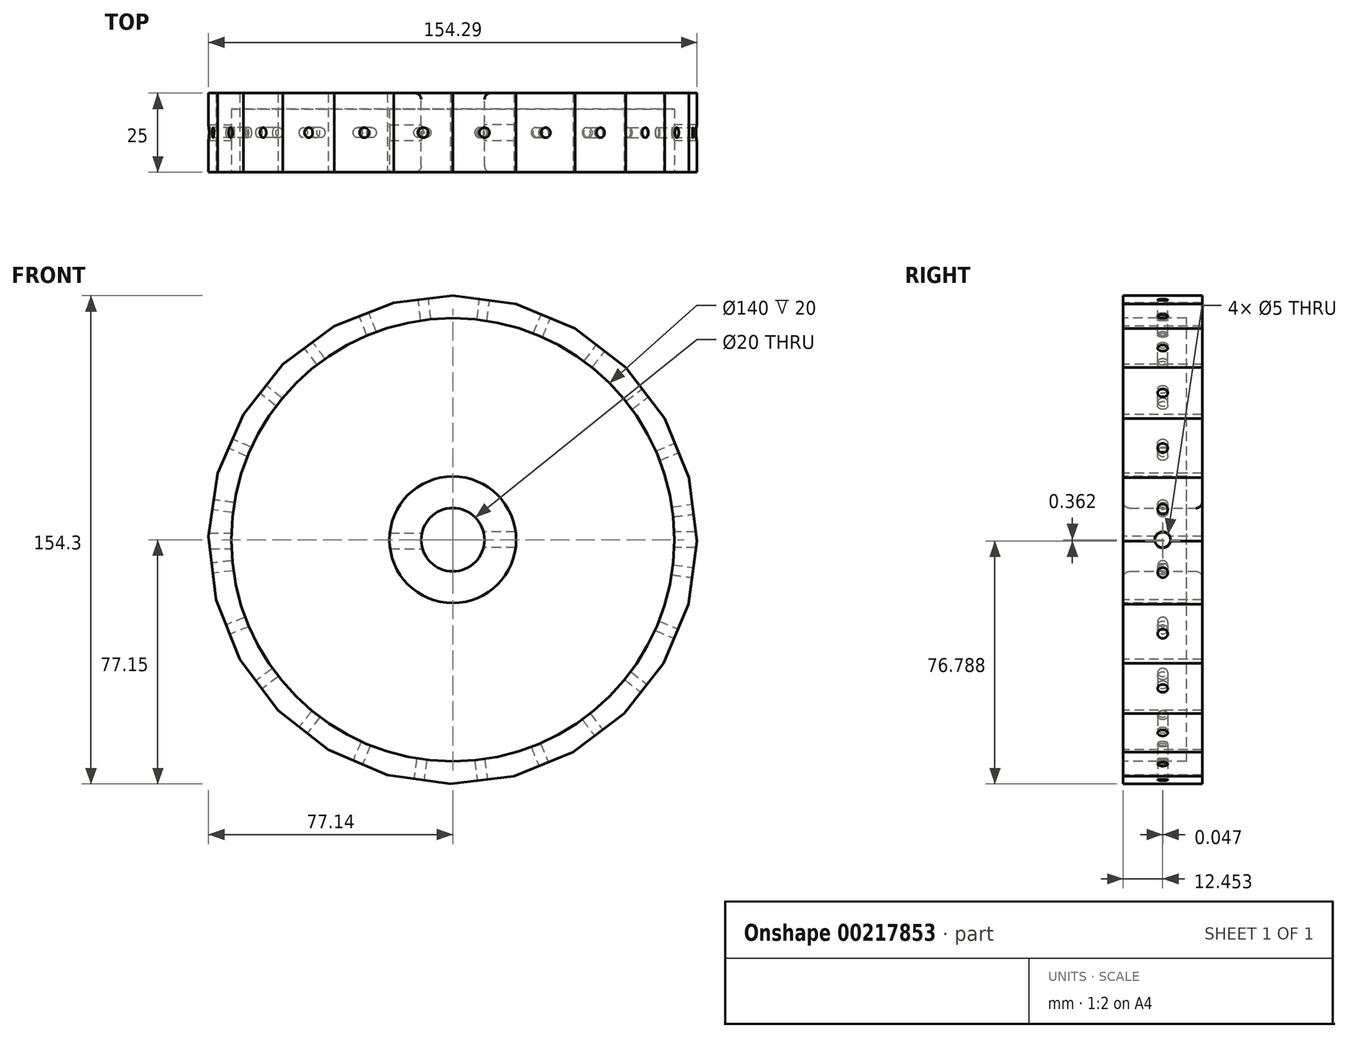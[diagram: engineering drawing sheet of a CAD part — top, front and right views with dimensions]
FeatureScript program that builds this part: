
annotation { "Feature Type Name" : "Feature", "Feature Type Description" : "" }
export const myFeature = defineFeature(function(context is Context, id is Id, definition is map)
    precondition{}
    {
        {
            var Q0;
            Q0=qCreatedBy(makeId("Front.planeOp"),FACE);
            var sketch = newSketch(context, id + "F0", { "sketchPlane" : qUnion([Q0])});
            skCircle(sketch, "E0", {"center": v(0, 0) * mm, "radius": 77.15 * mm});
            skCircle(sketch, "E1", {"center": v(0, 0) * mm, "radius": 10 * mm});
            skSolve(sketch);
        }
        {
            var Q0;
            Q0=qSketchRegion(id+"F0",true);
            extrude(context, id + "F1", {"entities" : qUnion([Q0]), "depth" : 25 * mm});
        }
        {
            var Q0;
            Q0=makeQuery(id+"F1.opExtrude","CAP_FACE",FACE,{"disambiguationData":[OSD([sQuery(id+"F0.wireOp",EDGE,"E0"),sQuery(id+"F0.wireOp",EDGE,"E1")])],"isStart":false});
            var sketch = newSketch(context, id + "F2", { "sketchPlane" : qUnion([Q0])});
            skLineSegment(sketch, "E2", {"start": v(0, 0) * mm, "end": v(0, 77.15) * mm});
            skLineSegment(sketch, "E3", {"start": v(0, 0) * mm, "end": v(20.03, 74.5) * mm});
            skLineSegment(sketch, "E4", {"start": v(0, 77.15) * mm, "end": v(20.03, 74.5) * mm});
            skLineSegment(sketch, "E5", {"start": v(0, 0) * mm, "end": v(38.68, 66.75) * mm});
            skLineSegment(sketch, "E6", {"start": v(20.03, 74.5) * mm, "end": v(38.68, 66.75) * mm});
            skLineSegment(sketch, "E7", {"start": v(0, 0) * mm, "end": v(54.68, 54.43) * mm});
            skLineSegment(sketch, "E8", {"start": v(38.68, 66.75) * mm, "end": v(54.68, 54.43) * mm});
            skLineSegment(sketch, "E9", {"start": v(0, 0) * mm, "end": v(66.93, 38.37) * mm});
            skLineSegment(sketch, "E10", {"start": v(54.68, 54.43) * mm, "end": v(66.93, 38.37) * mm});
            skLineSegment(sketch, "E11", {"start": v(0, 0) * mm, "end": v(74.6, 19.68) * mm});
            skLineSegment(sketch, "E12", {"start": v(74.6, 19.68) * mm, "end": v(66.93, 38.37) * mm});
            skLineSegment(sketch, "E13", {"start": v(0, 0) * mm, "end": v(77.15, -0.36) * mm});
            skLineSegment(sketch, "E14", {"start": v(77.15, -0.36) * mm, "end": v(74.6, 19.68) * mm});
            skLineSegment(sketch, "E15", {"start": v(0, 0) * mm, "end": v(74.41, -20.38) * mm});
            skLineSegment(sketch, "E16", {"start": v(74.41, -20.38) * mm, "end": v(77.15, -0.36) * mm});
            skLineSegment(sketch, "E17", {"start": v(0, 0) * mm, "end": v(66.57, -39) * mm});
            skLineSegment(sketch, "E18", {"start": v(66.57, -39) * mm, "end": v(74.41, -20.38) * mm});
            skLineSegment(sketch, "E19", {"start": v(0, 0) * mm, "end": v(54.17, -54.94) * mm});
            skLineSegment(sketch, "E20", {"start": v(54.17, -54.94) * mm, "end": v(66.57, -39) * mm});
            skLineSegment(sketch, "E21", {"start": v(0, 0) * mm, "end": v(38.05, -67.11) * mm});
            skLineSegment(sketch, "E22", {"start": v(38.05, -67.11) * mm, "end": v(54.17, -54.94) * mm});
            skLineSegment(sketch, "E23", {"start": v(0, 0) * mm, "end": v(19.33, -74.7) * mm});
            skLineSegment(sketch, "E24", {"start": v(19.33, -74.7) * mm, "end": v(38.05, -67.11) * mm});
            skLineSegment(sketch, "E25", {"start": v(0, 0) * mm, "end": v(-0.72, -77.15) * mm});
            skLineSegment(sketch, "E26", {"start": v(-0.72, -77.15) * mm, "end": v(19.33, -74.7) * mm});
            skLineSegment(sketch, "E27", {"start": v(0, 0) * mm, "end": v(-20.72, -74.31) * mm});
            skLineSegment(sketch, "E28", {"start": v(-20.72, -74.31) * mm, "end": v(-0.72, -77.15) * mm});
            skLineSegment(sketch, "E29", {"start": v(0, 0) * mm, "end": v(-39.3, -66.39) * mm});
            skLineSegment(sketch, "E30", {"start": v(-39.3, -66.39) * mm, "end": v(-20.72, -74.31) * mm});
            skLineSegment(sketch, "E31", {"start": v(0, 0) * mm, "end": v(-55.19, -53.9) * mm});
            skLineSegment(sketch, "E32", {"start": v(-55.19, -53.9) * mm, "end": v(-39.3, -66.39) * mm});
            skLineSegment(sketch, "E33", {"start": v(0, 0) * mm, "end": v(-67.3, -37.74) * mm});
            skLineSegment(sketch, "E34", {"start": v(-67.3, -37.74) * mm, "end": v(-55.19, -53.9) * mm});
            skLineSegment(sketch, "E35", {"start": v(0, 0) * mm, "end": v(-74.78, -18.98) * mm});
            skLineSegment(sketch, "E36", {"start": v(-74.78, -18.98) * mm, "end": v(-67.3, -37.74) * mm});
            skLineSegment(sketch, "E37", {"start": v(0, 0) * mm, "end": v(-77.14, 1.09) * mm});
            skLineSegment(sketch, "E38", {"start": v(-77.14, 1.09) * mm, "end": v(-74.78, -18.98) * mm});
            skLineSegment(sketch, "E39", {"start": v(0, 0) * mm, "end": v(-74.22, 21.07) * mm});
            skLineSegment(sketch, "E40", {"start": v(-74.22, 21.07) * mm, "end": v(-77.14, 1.09) * mm});
            skLineSegment(sketch, "E41", {"start": v(0, 0) * mm, "end": v(-66.2, 39.62) * mm});
            skLineSegment(sketch, "E42", {"start": v(-66.2, 39.62) * mm, "end": v(-74.22, 21.07) * mm});
            skLineSegment(sketch, "E43", {"start": v(0, 0) * mm, "end": v(-53.65, 55.44) * mm});
            skLineSegment(sketch, "E44", {"start": v(-53.65, 55.44) * mm, "end": v(-66.2, 39.62) * mm});
            skLineSegment(sketch, "E45", {"start": v(0, 0) * mm, "end": v(-37.42, 67.47) * mm});
            skLineSegment(sketch, "E46", {"start": v(-37.42, 67.47) * mm, "end": v(-53.65, 55.44) * mm});
            skLineSegment(sketch, "E47", {"start": v(0, 0) * mm, "end": v(-18.62, 74.87) * mm});
            skLineSegment(sketch, "E48", {"start": v(-18.62, 74.87) * mm, "end": v(-37.42, 67.47) * mm});
            skLineSegment(sketch, "E49", {"start": v(-18.62, 74.87) * mm, "end": v(0, 77.15) * mm});
            skSolve(sketch);
        }
        {
            var Q0;
            {var subQ0=sQuery(id+"F2.wireOp",EDGE,"E4");Q0=makeQuery(id+"F2.imprint","IMPRINT",FACE,{"disambiguationData":[TD([[makeQuery(id+"F2.imprint","IMPRINT",EDGE,{"derivedFrom":subQ0}),1.0]])]});}
            var Q1;
            {var subQ0=sQuery(id+"F2.wireOp",EDGE,"E6");Q1=makeQuery(id+"F2.imprint","IMPRINT",FACE,{"disambiguationData":[TD([[makeQuery(id+"F2.imprint","IMPRINT",EDGE,{"derivedFrom":subQ0}),1.0]])]});}
            var Q2;
            {var subQ0=sQuery(id+"F2.wireOp",EDGE,"E8");Q2=makeQuery(id+"F2.imprint","IMPRINT",FACE,{"disambiguationData":[TD([[makeQuery(id+"F2.imprint","IMPRINT",EDGE,{"derivedFrom":subQ0}),1.0]])]});}
            var Q3;
            {var subQ0=sQuery(id+"F2.wireOp",EDGE,"E10");Q3=makeQuery(id+"F2.imprint","IMPRINT",FACE,{"disambiguationData":[TD([[makeQuery(id+"F2.imprint","IMPRINT",EDGE,{"derivedFrom":subQ0}),1.0]])]});}
            var Q4;
            {var subQ0=sQuery(id+"F2.wireOp",EDGE,"E12");Q4=makeQuery(id+"F2.imprint","IMPRINT",FACE,{"disambiguationData":[TD([[makeQuery(id+"F2.imprint","IMPRINT",EDGE,{"derivedFrom":subQ0}),-1.0]])]});}
            var Q5;
            {var subQ0=sQuery(id+"F2.wireOp",EDGE,"E14");Q5=makeQuery(id+"F2.imprint","IMPRINT",FACE,{"disambiguationData":[TD([[makeQuery(id+"F2.imprint","IMPRINT",EDGE,{"derivedFrom":subQ0}),-1.0]])]});}
            var Q6;
            {var subQ0=sQuery(id+"F2.wireOp",EDGE,"E16");Q6=makeQuery(id+"F2.imprint","IMPRINT",FACE,{"disambiguationData":[TD([[makeQuery(id+"F2.imprint","IMPRINT",EDGE,{"derivedFrom":subQ0}),-1.0]])]});}
            var Q7;
            {var subQ0=sQuery(id+"F2.wireOp",EDGE,"E18");Q7=makeQuery(id+"F2.imprint","IMPRINT",FACE,{"disambiguationData":[TD([[makeQuery(id+"F2.imprint","IMPRINT",EDGE,{"derivedFrom":subQ0}),-1.0]])]});}
            var Q8;
            {var subQ0=sQuery(id+"F2.wireOp",EDGE,"E20");Q8=makeQuery(id+"F2.imprint","IMPRINT",FACE,{"disambiguationData":[TD([[makeQuery(id+"F2.imprint","IMPRINT",EDGE,{"derivedFrom":subQ0}),-1.0]])]});}
            var Q9;
            {var subQ0=sQuery(id+"F2.wireOp",EDGE,"E22");Q9=makeQuery(id+"F2.imprint","IMPRINT",FACE,{"disambiguationData":[TD([[makeQuery(id+"F2.imprint","IMPRINT",EDGE,{"derivedFrom":subQ0}),-1.0]])]});}
            var Q10;
            {var subQ0=sQuery(id+"F2.wireOp",EDGE,"E24");Q10=makeQuery(id+"F2.imprint","IMPRINT",FACE,{"disambiguationData":[TD([[makeQuery(id+"F2.imprint","IMPRINT",EDGE,{"derivedFrom":subQ0}),-1.0]])]});}
            var Q11;
            {var subQ0=sQuery(id+"F2.wireOp",EDGE,"E26");Q11=makeQuery(id+"F2.imprint","IMPRINT",FACE,{"disambiguationData":[TD([[makeQuery(id+"F2.imprint","IMPRINT",EDGE,{"derivedFrom":subQ0}),-1.0]])]});}
            var Q12;
            {var subQ0=sQuery(id+"F2.wireOp",EDGE,"E28");Q12=makeQuery(id+"F2.imprint","IMPRINT",FACE,{"disambiguationData":[TD([[makeQuery(id+"F2.imprint","IMPRINT",EDGE,{"derivedFrom":subQ0}),-1.0]])]});}
            var Q13;
            {var subQ0=sQuery(id+"F2.wireOp",EDGE,"E30");Q13=makeQuery(id+"F2.imprint","IMPRINT",FACE,{"disambiguationData":[TD([[makeQuery(id+"F2.imprint","IMPRINT",EDGE,{"derivedFrom":subQ0}),-1.0]])]});}
            var Q14;
            {var subQ0=sQuery(id+"F2.wireOp",EDGE,"E32");Q14=makeQuery(id+"F2.imprint","IMPRINT",FACE,{"disambiguationData":[TD([[makeQuery(id+"F2.imprint","IMPRINT",EDGE,{"derivedFrom":subQ0}),-1.0]])]});}
            var Q15;
            {var subQ0=sQuery(id+"F2.wireOp",EDGE,"E34");Q15=makeQuery(id+"F2.imprint","IMPRINT",FACE,{"disambiguationData":[TD([[makeQuery(id+"F2.imprint","IMPRINT",EDGE,{"derivedFrom":subQ0}),-1.0]])]});}
            var Q16;
            {var subQ0=sQuery(id+"F2.wireOp",EDGE,"E36");Q16=makeQuery(id+"F2.imprint","IMPRINT",FACE,{"disambiguationData":[TD([[makeQuery(id+"F2.imprint","IMPRINT",EDGE,{"derivedFrom":subQ0}),-1.0]])]});}
            var Q17;
            {var subQ0=sQuery(id+"F2.wireOp",EDGE,"E38");Q17=makeQuery(id+"F2.imprint","IMPRINT",FACE,{"disambiguationData":[TD([[makeQuery(id+"F2.imprint","IMPRINT",EDGE,{"derivedFrom":subQ0}),-1.0]])]});}
            var Q18;
            {var subQ0=sQuery(id+"F2.wireOp",EDGE,"E40");Q18=makeQuery(id+"F2.imprint","IMPRINT",FACE,{"disambiguationData":[TD([[makeQuery(id+"F2.imprint","IMPRINT",EDGE,{"derivedFrom":subQ0}),-1.0]])]});}
            var Q19;
            {var subQ0=sQuery(id+"F2.wireOp",EDGE,"E42");Q19=makeQuery(id+"F2.imprint","IMPRINT",FACE,{"disambiguationData":[TD([[makeQuery(id+"F2.imprint","IMPRINT",EDGE,{"derivedFrom":subQ0}),-1.0]])]});}
            var Q20;
            {var subQ0=sQuery(id+"F2.wireOp",EDGE,"E44");Q20=makeQuery(id+"F2.imprint","IMPRINT",FACE,{"disambiguationData":[TD([[makeQuery(id+"F2.imprint","IMPRINT",EDGE,{"derivedFrom":subQ0}),-1.0]])]});}
            var Q21;
            {var subQ0=sQuery(id+"F2.wireOp",EDGE,"E46");Q21=makeQuery(id+"F2.imprint","IMPRINT",FACE,{"disambiguationData":[TD([[makeQuery(id+"F2.imprint","IMPRINT",EDGE,{"derivedFrom":subQ0}),-1.0]])]});}
            var Q22;
            {var subQ0=sQuery(id+"F2.wireOp",EDGE,"E48");Q22=makeQuery(id+"F2.imprint","IMPRINT",FACE,{"disambiguationData":[TD([[makeQuery(id+"F2.imprint","IMPRINT",EDGE,{"derivedFrom":subQ0}),-1.0]])]});}
            var Q23;
            {var subQ0=sQuery(id+"F2.wireOp",EDGE,"E49");Q23=makeQuery(id+"F2.imprint","IMPRINT",FACE,{"disambiguationData":[TD([[makeQuery(id+"F2.imprint","IMPRINT",EDGE,{"derivedFrom":subQ0}),1.0]])]});}
            extrude(context, id + "F3", {"entities" : qUnion([Q0, Q1, Q2, Q3, Q4, Q5, Q6, Q7, Q8, Q9, Q10, Q11, Q12, Q13, Q14, Q15, Q16, Q17, Q18, Q19, Q20, Q21, Q22, Q23]), "operationType" : NewBodyOperationType.REMOVE, "oppositeDirection" : true, "depth" : 25 * mm});
        }
        {
            var Q0;
            Q0=makeQuery(id+"F1.opExtrude","CAP_FACE",FACE,{"disambiguationData":[OSD([sQuery(id+"F0.wireOp",EDGE,"E0"),sQuery(id+"F0.wireOp",EDGE,"E1")])],"isStart":false});
            var sketch = newSketch(context, id + "F4", { "sketchPlane" : qUnion([Q0])});
            skCircle(sketch, "E50", {"center": v(0, 0) * mm, "radius": 10 * mm});
            skCircle(sketch, "E51", {"center": v(0, 0) * mm, "radius": 20 * mm});
            skCircle(sketch, "E52", {"center": v(0, 0) * mm, "radius": 70 * mm});
            skSolve(sketch);
        }
        {
            var Q0;
            Q0=makeQuery(id+"F4.imprint","IMPRINT",FACE,{"disambiguationData":[TD([[makeQuery(id+"F4.imprint","IMPRINT",EDGE,{"derivedFrom":sQuery(id+"F4.wireOp",EDGE,"E51")}),-1.0]])]});
            extrude(context, id + "F5", {"entities" : qUnion([Q0]), "operationType" : NewBodyOperationType.REMOVE, "oppositeDirection" : true, "depth" : 20 * mm});
        }
        {
            var Q0;
            Q0=makeQuery(id+"F1.opExtrude","CAP_EDGE",EDGE,{"disambiguationData":[OSD([sQuery(id+"F0.wireOp",EDGE,"E1")])],"isStart":true});
            var Q1;
            Q1=makeQuery(id+"F1.opExtrude","CAP_EDGE",EDGE,{"disambiguationData":[OSD([sQuery(id+"F0.wireOp",EDGE,"E1")])],"isStart":false});
            fillet(context, id + "F6", {"entities" : qUnion([Q0, Q1]), "radius" : 2 * mm, "tangentPropagation" : true, "allowEdgeOverflow" : false});
        }
        {
            var Q0;
            Q0=makeQuery(id+"F3.boolean.opBoolean","COPY",FACE,{"derivedFrom":makeQuery(id+"F3.opExtrude","SWEPT_FACE",FACE,{"disambiguationData":[OSD([sQuery(id+"F2.wireOp",EDGE,"E14")])]})});
            var sketch = newSketch(context, id + "F7", { "sketchPlane" : qUnion([Q0])});
            skCircle(sketch, "E53", {"center": v(-12.5, 0) * mm, "radius": 1.75 * mm});
            skPoint(sketch, "E53.centerSnap0", {"position": v(-25, 0) * mm});
            skSolve(sketch);
        }
        {
            var Q0;
            Q0=sQuery(id+"F7.wireOp",VERTEX,"E53.center");
            var Q1;
            Q1=makeQuery(id+"F1.opExtrude","SWEPT_BODY",BODY,{"disambiguationData":[OSD([sQuery(id+"F0.wireOp",EDGE,"E0"),sQuery(id+"F0.wireOp",EDGE,"E1")])]});
            hole(context, id + "F8", {"style" : HoleStyle.SIMPLE, "endStyle" : HoleEndStyle.BLIND, "standardTappedOrClearance" : lookupTablePath({ "standard" : "ISO", "engagement" : "75%", "pitch" : "0.75 mm", "size" : "M4", "type" : "Tapped" }), "standardBlindInLast" : lookupTablePath({ "standard" : "ISO", "engagement" : "75%", "pitch" : "0.75 mm", "size" : "M4", "type" : "Tapped" }), "holeDiameter" : 3.2 * mm, "holeDepth" : 20 * mm, "startFromSketch" : true, "locations" : qUnion([Q0]), "scope" : qUnion([Q1])});
        }
        {
            var Q0;
            Q0=makeQuery(id+"F3.boolean.opBoolean","COPY",FACE,{"derivedFrom":makeQuery(id+"F3.opExtrude","SWEPT_FACE",FACE,{"disambiguationData":[OSD([sQuery(id+"F2.wireOp",EDGE,"E16")])]})});
            var sketch = newSketch(context, id + "F9", { "sketchPlane" : qUnion([Q0])});
            skCircle(sketch, "E54", {"center": v(-12.5, 0) * mm, "radius": 1.75 * mm});
            skSolve(sketch);
        }
        {
            var Q0;
            Q0=sQuery(id+"F9.wireOp",VERTEX,"E54.center");
            var Q1;
            Q1=makeQuery(id+"F1.opExtrude","SWEPT_BODY",BODY,{"disambiguationData":[OSD([sQuery(id+"F0.wireOp",EDGE,"E0"),sQuery(id+"F0.wireOp",EDGE,"E1")])]});
            hole(context, id + "F10", {"style" : HoleStyle.SIMPLE, "endStyle" : HoleEndStyle.BLIND, "standardTappedOrClearance" : lookupTablePath({ "standard" : "ISO", "engagement" : "75%", "pitch" : "0.75 mm", "size" : "M4", "type" : "Tapped" }), "standardBlindInLast" : lookupTablePath({ "standard" : "ISO", "engagement" : "75%", "pitch" : "0.75 mm", "size" : "M4", "type" : "Tapped" }), "holeDiameter" : 3.2 * mm, "holeDepth" : 20 * mm, "startFromSketch" : true, "locations" : qUnion([Q0]), "scope" : qUnion([Q1])});
        }
        {
            var Q0;
            Q0=makeQuery(id+"F3.boolean.opBoolean","COPY",FACE,{"derivedFrom":makeQuery(id+"F3.opExtrude","SWEPT_FACE",FACE,{"disambiguationData":[OSD([sQuery(id+"F2.wireOp",EDGE,"E18")])]})});
            var sketch = newSketch(context, id + "F11", { "sketchPlane" : qUnion([Q0])});
            skCircle(sketch, "E55", {"center": v(-12.5, 0) * mm, "radius": 1.75 * mm});
            skSolve(sketch);
        }
        {
            var Q0;
            Q0=sQuery(id+"F11.wireOp",VERTEX,"E55.center");
            var Q1;
            Q1=makeQuery(id+"F1.opExtrude","SWEPT_BODY",BODY,{"disambiguationData":[OSD([sQuery(id+"F0.wireOp",EDGE,"E0"),sQuery(id+"F0.wireOp",EDGE,"E1")])]});
            hole(context, id + "F12", {"style" : HoleStyle.SIMPLE, "endStyle" : HoleEndStyle.BLIND, "standardTappedOrClearance" : lookupTablePath({ "standard" : "ISO", "engagement" : "75%", "pitch" : "0.75 mm", "size" : "M4", "type" : "Tapped" }), "standardBlindInLast" : lookupTablePath({ "standard" : "ISO", "engagement" : "75%", "pitch" : "0.75 mm", "size" : "M4", "type" : "Tapped" }), "holeDiameter" : 3.2 * mm, "holeDepth" : 20 * mm, "startFromSketch" : true, "locations" : qUnion([Q0]), "scope" : qUnion([Q1])});
        }
        {
            var Q0;
            Q0=makeQuery(id+"F3.boolean.opBoolean","COPY",FACE,{"derivedFrom":makeQuery(id+"F3.opExtrude","SWEPT_FACE",FACE,{"disambiguationData":[OSD([sQuery(id+"F2.wireOp",EDGE,"E20")])]})});
            var sketch = newSketch(context, id + "F13", { "sketchPlane" : qUnion([Q0])});
            skCircle(sketch, "E56", {"center": v(-12.5, 0) * mm, "radius": 1.75 * mm});
            skSolve(sketch);
        }
        {
            var Q0;
            Q0=sQuery(id+"F13.wireOp",VERTEX,"E56.center");
            var Q1;
            Q1=makeQuery(id+"F1.opExtrude","SWEPT_BODY",BODY,{"disambiguationData":[OSD([sQuery(id+"F0.wireOp",EDGE,"E0"),sQuery(id+"F0.wireOp",EDGE,"E1")])]});
            hole(context, id + "F14", {"style" : HoleStyle.SIMPLE, "endStyle" : HoleEndStyle.BLIND, "standardTappedOrClearance" : lookupTablePath({ "standard" : "ISO", "engagement" : "75%", "pitch" : "0.75 mm", "size" : "M4", "type" : "Tapped" }), "standardBlindInLast" : lookupTablePath({ "standard" : "ISO", "engagement" : "75%", "pitch" : "0.75 mm", "size" : "M4", "type" : "Tapped" }), "holeDiameter" : 3.2 * mm, "holeDepth" : 20 * mm, "startFromSketch" : true, "locations" : qUnion([Q0]), "scope" : qUnion([Q1])});
        }
        {
            var Q0;
            Q0=makeQuery(id+"F3.boolean.opBoolean","COPY",FACE,{"derivedFrom":makeQuery(id+"F3.opExtrude","SWEPT_FACE",FACE,{"disambiguationData":[OSD([sQuery(id+"F2.wireOp",EDGE,"E22")])]})});
            var sketch = newSketch(context, id + "F15", { "sketchPlane" : qUnion([Q0])});
            skCircle(sketch, "E57", {"center": v(0, 12.5) * mm, "radius": 1.75 * mm});
            skPoint(sketch, "E57.centerSnap0", {"position": v(-10.1, 12.5) * mm});
            skSolve(sketch);
        }
        {
            var Q0;
            Q0=sQuery(id+"F15.wireOp",VERTEX,"E57.center");
            var Q1;
            Q1=makeQuery(id+"F1.opExtrude","SWEPT_BODY",BODY,{"disambiguationData":[OSD([sQuery(id+"F0.wireOp",EDGE,"E0"),sQuery(id+"F0.wireOp",EDGE,"E1")])]});
            hole(context, id + "F16", {"style" : HoleStyle.SIMPLE, "endStyle" : HoleEndStyle.BLIND, "standardTappedOrClearance" : lookupTablePath({ "standard" : "ISO", "engagement" : "75%", "pitch" : "0.75 mm", "size" : "M4", "type" : "Tapped" }), "standardBlindInLast" : lookupTablePath({ "standard" : "ISO", "engagement" : "75%", "pitch" : "0.75 mm", "size" : "M4", "type" : "Tapped" }), "holeDiameter" : 3.2 * mm, "holeDepth" : 20 * mm, "startFromSketch" : true, "locations" : qUnion([Q0]), "scope" : qUnion([Q1])});
        }
        {
            var Q0;
            Q0=makeQuery(id+"F3.boolean.opBoolean","COPY",FACE,{"derivedFrom":makeQuery(id+"F3.opExtrude","SWEPT_FACE",FACE,{"disambiguationData":[OSD([sQuery(id+"F2.wireOp",EDGE,"E24")])]})});
            var sketch = newSketch(context, id + "F17", { "sketchPlane" : qUnion([Q0])});
            skCircle(sketch, "E58", {"center": v(0, 12.5) * mm, "radius": 1.75 * mm});
            skSolve(sketch);
        }
        {
            var Q0;
            Q0=sQuery(id+"F17.wireOp",VERTEX,"E58.center");
            var Q1;
            Q1=makeQuery(id+"F1.opExtrude","SWEPT_BODY",BODY,{"disambiguationData":[OSD([sQuery(id+"F0.wireOp",EDGE,"E0"),sQuery(id+"F0.wireOp",EDGE,"E1")])]});
            hole(context, id + "F18", {"style" : HoleStyle.SIMPLE, "endStyle" : HoleEndStyle.BLIND, "standardTappedOrClearance" : lookupTablePath({ "standard" : "ISO", "engagement" : "75%", "pitch" : "0.75 mm", "size" : "M4", "type" : "Tapped" }), "standardBlindInLast" : lookupTablePath({ "standard" : "ISO", "engagement" : "75%", "pitch" : "0.75 mm", "size" : "M4", "type" : "Tapped" }), "holeDiameter" : 3.2 * mm, "holeDepth" : 20 * mm, "startFromSketch" : true, "locations" : qUnion([Q0]), "scope" : qUnion([Q1])});
        }
        {
            var Q0;
            Q0=makeQuery(id+"F3.boolean.opBoolean","COPY",FACE,{"derivedFrom":makeQuery(id+"F3.opExtrude","SWEPT_FACE",FACE,{"disambiguationData":[OSD([sQuery(id+"F2.wireOp",EDGE,"E26")])]})});
            var sketch = newSketch(context, id + "F19", { "sketchPlane" : qUnion([Q0])});
            skCircle(sketch, "E59", {"center": v(0, 12.5) * mm, "radius": 1.75 * mm});
            skSolve(sketch);
        }
        {
            var Q0;
            Q0=sQuery(id+"F19.wireOp",VERTEX,"E59.center");
            var Q1;
            Q1=makeQuery(id+"F1.opExtrude","SWEPT_BODY",BODY,{"disambiguationData":[OSD([sQuery(id+"F0.wireOp",EDGE,"E0"),sQuery(id+"F0.wireOp",EDGE,"E1")])]});
            hole(context, id + "F20", {"style" : HoleStyle.SIMPLE, "endStyle" : HoleEndStyle.BLIND, "standardTappedOrClearance" : lookupTablePath({ "standard" : "ISO", "engagement" : "75%", "pitch" : "0.75 mm", "size" : "M4", "type" : "Tapped" }), "standardBlindInLast" : lookupTablePath({ "standard" : "ISO", "engagement" : "75%", "pitch" : "0.75 mm", "size" : "M4", "type" : "Tapped" }), "holeDiameter" : 3.2 * mm, "holeDepth" : 20 * mm, "startFromSketch" : true, "locations" : qUnion([Q0]), "scope" : qUnion([Q1])});
        }
        {
            var Q0;
            Q0=makeQuery(id+"F3.boolean.opBoolean","COPY",FACE,{"derivedFrom":makeQuery(id+"F3.opExtrude","SWEPT_FACE",FACE,{"disambiguationData":[OSD([sQuery(id+"F2.wireOp",EDGE,"E28")])]})});
            var sketch = newSketch(context, id + "F21", { "sketchPlane" : qUnion([Q0])});
            skCircle(sketch, "E60", {"center": v(0, 12.5) * mm, "radius": 1.75 * mm});
            skPoint(sketch, "E60.centerSnap0", {"position": v(-10.1, 12.5) * mm});
            skSolve(sketch);
        }
        {
            var Q0;
            Q0=sQuery(id+"F21.wireOp",VERTEX,"E60.center");
            var Q1;
            Q1=makeQuery(id+"F1.opExtrude","SWEPT_BODY",BODY,{"disambiguationData":[OSD([sQuery(id+"F0.wireOp",EDGE,"E0"),sQuery(id+"F0.wireOp",EDGE,"E1")])]});
            hole(context, id + "F22", {"style" : HoleStyle.SIMPLE, "endStyle" : HoleEndStyle.BLIND, "standardTappedOrClearance" : lookupTablePath({ "standard" : "ISO", "engagement" : "75%", "pitch" : "0.75 mm", "size" : "M4", "type" : "Tapped" }), "standardBlindInLast" : lookupTablePath({ "standard" : "ISO", "engagement" : "75%", "pitch" : "0.75 mm", "size" : "M4", "type" : "Tapped" }), "holeDiameter" : 3.2 * mm, "holeDepth" : 20 * mm, "startFromSketch" : true, "locations" : qUnion([Q0]), "scope" : qUnion([Q1])});
        }
        {
            var Q0;
            Q0=makeQuery(id+"F3.boolean.opBoolean","COPY",FACE,{"derivedFrom":makeQuery(id+"F3.opExtrude","SWEPT_FACE",FACE,{"disambiguationData":[OSD([sQuery(id+"F2.wireOp",EDGE,"E30")])]})});
            var sketch = newSketch(context, id + "F23", { "sketchPlane" : qUnion([Q0])});
            skCircle(sketch, "E61", {"center": v(0, 12.5) * mm, "radius": 1.75 * mm});
            skPoint(sketch, "E61.centerSnap0", {"position": v(10.1, 12.5) * mm});
            skSolve(sketch);
        }
        {
            var Q0;
            Q0=sQuery(id+"F23.wireOp",VERTEX,"E61.center");
            var Q1;
            Q1=makeQuery(id+"F1.opExtrude","SWEPT_BODY",BODY,{"disambiguationData":[OSD([sQuery(id+"F0.wireOp",EDGE,"E0"),sQuery(id+"F0.wireOp",EDGE,"E1")])]});
            hole(context, id + "F24", {"style" : HoleStyle.SIMPLE, "endStyle" : HoleEndStyle.BLIND, "standardTappedOrClearance" : lookupTablePath({ "standard" : "ISO", "engagement" : "75%", "pitch" : "0.75 mm", "size" : "M4", "type" : "Tapped" }), "standardBlindInLast" : lookupTablePath({ "standard" : "ISO", "engagement" : "75%", "pitch" : "0.75 mm", "size" : "M4", "type" : "Tapped" }), "holeDiameter" : 3.2 * mm, "holeDepth" : 20 * mm, "startFromSketch" : true, "locations" : qUnion([Q0]), "scope" : qUnion([Q1])});
        }
        {
            var Q0;
            Q0=makeQuery(id+"F3.boolean.opBoolean","COPY",FACE,{"derivedFrom":makeQuery(id+"F3.opExtrude","SWEPT_FACE",FACE,{"disambiguationData":[OSD([sQuery(id+"F2.wireOp",EDGE,"E32")])]})});
            var sketch = newSketch(context, id + "F25", { "sketchPlane" : qUnion([Q0])});
            skCircle(sketch, "E62", {"center": v(0, 12.5) * mm, "radius": 1.75 * mm});
            skPoint(sketch, "E62.centerSnap0", {"position": v(10.1, 12.5) * mm});
            skSolve(sketch);
        }
        {
            var Q0;
            Q0=sQuery(id+"F25.wireOp",VERTEX,"E62.center");
            var Q1;
            Q1=makeQuery(id+"F1.opExtrude","SWEPT_BODY",BODY,{"disambiguationData":[OSD([sQuery(id+"F0.wireOp",EDGE,"E0"),sQuery(id+"F0.wireOp",EDGE,"E1")])]});
            hole(context, id + "F26", {"style" : HoleStyle.SIMPLE, "endStyle" : HoleEndStyle.BLIND, "standardTappedOrClearance" : lookupTablePath({ "standard" : "ISO", "engagement" : "75%", "pitch" : "0.75 mm", "size" : "M4", "type" : "Tapped" }), "standardBlindInLast" : lookupTablePath({ "standard" : "ISO", "engagement" : "75%", "pitch" : "0.75 mm", "size" : "M4", "type" : "Tapped" }), "holeDiameter" : 3.2 * mm, "holeDepth" : 20 * mm, "startFromSketch" : true, "locations" : qUnion([Q0]), "scope" : qUnion([Q1])});
        }
        {
            var Q0;
            Q0=makeQuery(id+"F3.boolean.opBoolean","COPY",FACE,{"derivedFrom":makeQuery(id+"F3.opExtrude","SWEPT_FACE",FACE,{"disambiguationData":[OSD([sQuery(id+"F2.wireOp",EDGE,"E34")])]})});
            var sketch = newSketch(context, id + "F27", { "sketchPlane" : qUnion([Q0])});
            skCircle(sketch, "E63", {"center": v(12.5, 0) * mm, "radius": 1.75 * mm});
            skPoint(sketch, "E63.centerSnap0", {"position": v(12.5, -10.1) * mm});
            skPoint(sketch, "E63.centerSnap1", {"position": v(0, 0) * mm});
            skSolve(sketch);
        }
        {
            var Q0;
            Q0=sQuery(id+"F27.wireOp",VERTEX,"E63.center");
            var Q1;
            Q1=makeQuery(id+"F1.opExtrude","SWEPT_BODY",BODY,{"disambiguationData":[OSD([sQuery(id+"F0.wireOp",EDGE,"E0"),sQuery(id+"F0.wireOp",EDGE,"E1")])]});
            hole(context, id + "F28", {"style" : HoleStyle.SIMPLE, "endStyle" : HoleEndStyle.BLIND, "standardTappedOrClearance" : lookupTablePath({ "standard" : "ISO", "engagement" : "75%", "pitch" : "0.75 mm", "size" : "M4", "type" : "Tapped" }), "standardBlindInLast" : lookupTablePath({ "standard" : "ISO", "engagement" : "75%", "pitch" : "0.75 mm", "size" : "M4", "type" : "Tapped" }), "holeDiameter" : 3.2 * mm, "holeDepth" : 20 * mm, "startFromSketch" : true, "locations" : qUnion([Q0]), "scope" : qUnion([Q1])});
        }
        {
            var Q0;
            Q0=makeQuery(id+"F3.boolean.opBoolean","COPY",FACE,{"derivedFrom":makeQuery(id+"F3.opExtrude","SWEPT_FACE",FACE,{"disambiguationData":[OSD([sQuery(id+"F2.wireOp",EDGE,"E36")])]})});
            var sketch = newSketch(context, id + "F29", { "sketchPlane" : qUnion([Q0])});
            skCircle(sketch, "E64", {"center": v(12.5, 0) * mm, "radius": 1.75 * mm});
            skPoint(sketch, "E64.centerSnap0", {"position": v(12.5, -10.1) * mm});
            skSolve(sketch);
        }
        {
            var Q0;
            Q0=sQuery(id+"F29.wireOp",VERTEX,"E64.center");
            var Q1;
            Q1=makeQuery(id+"F1.opExtrude","SWEPT_BODY",BODY,{"disambiguationData":[OSD([sQuery(id+"F0.wireOp",EDGE,"E0"),sQuery(id+"F0.wireOp",EDGE,"E1")])]});
            hole(context, id + "F30", {"style" : HoleStyle.SIMPLE, "endStyle" : HoleEndStyle.BLIND, "standardTappedOrClearance" : lookupTablePath({ "standard" : "ISO", "engagement" : "75%", "pitch" : "0.75 mm", "size" : "M4", "type" : "Tapped" }), "standardBlindInLast" : lookupTablePath({ "standard" : "ISO", "engagement" : "75%", "pitch" : "0.75 mm", "size" : "M4", "type" : "Tapped" }), "holeDiameter" : 3.2 * mm, "holeDepth" : 20 * mm, "startFromSketch" : true, "locations" : qUnion([Q0]), "scope" : qUnion([Q1])});
        }
        {
            var Q0;
            Q0=makeQuery(id+"F3.boolean.opBoolean","COPY",FACE,{"derivedFrom":makeQuery(id+"F3.opExtrude","SWEPT_FACE",FACE,{"disambiguationData":[OSD([sQuery(id+"F2.wireOp",EDGE,"E38")])]})});
            var sketch = newSketch(context, id + "F31", { "sketchPlane" : qUnion([Q0])});
            skCircle(sketch, "E65", {"center": v(12.5, 0) * mm, "radius": 1.75 * mm});
            skPoint(sketch, "E65.centerSnap0", {"position": v(12.5, -10.1) * mm});
            skSolve(sketch);
        }
        {
            var Q0;
            Q0=sQuery(id+"F31.wireOp",VERTEX,"E65.center");
            var Q1;
            Q1=makeQuery(id+"F1.opExtrude","SWEPT_BODY",BODY,{"disambiguationData":[OSD([sQuery(id+"F0.wireOp",EDGE,"E0"),sQuery(id+"F0.wireOp",EDGE,"E1")])]});
            hole(context, id + "F32", {"style" : HoleStyle.SIMPLE, "endStyle" : HoleEndStyle.BLIND, "standardTappedOrClearance" : lookupTablePath({ "standard" : "ISO", "engagement" : "75%", "pitch" : "0.75 mm", "size" : "M4", "type" : "Tapped" }), "standardBlindInLast" : lookupTablePath({ "standard" : "ISO", "engagement" : "75%", "pitch" : "0.75 mm", "size" : "M4", "type" : "Tapped" }), "holeDiameter" : 3.2 * mm, "holeDepth" : 20 * mm, "startFromSketch" : true, "locations" : qUnion([Q0]), "scope" : qUnion([Q1])});
        }
        {
            var Q0;
            Q0=makeQuery(id+"F3.boolean.opBoolean","COPY",FACE,{"derivedFrom":makeQuery(id+"F3.opExtrude","SWEPT_FACE",FACE,{"disambiguationData":[OSD([sQuery(id+"F2.wireOp",EDGE,"E40")])]})});
            var sketch = newSketch(context, id + "F33", { "sketchPlane" : qUnion([Q0])});
            skCircle(sketch, "E66", {"center": v(12.5, 0) * mm, "radius": 1.75 * mm});
            skPoint(sketch, "E66.centerSnap0", {"position": v(12.5, -10.1) * mm});
            skSolve(sketch);
        }
        {
            var Q0;
            Q0=sQuery(id+"F33.wireOp",VERTEX,"E66.center");
            var Q1;
            Q1=makeQuery(id+"F1.opExtrude","SWEPT_BODY",BODY,{"disambiguationData":[OSD([sQuery(id+"F0.wireOp",EDGE,"E0"),sQuery(id+"F0.wireOp",EDGE,"E1")])]});
            hole(context, id + "F34", {"style" : HoleStyle.SIMPLE, "endStyle" : HoleEndStyle.BLIND, "standardTappedOrClearance" : lookupTablePath({ "standard" : "ISO", "engagement" : "75%", "pitch" : "0.75 mm", "size" : "M4", "type" : "Tapped" }), "standardBlindInLast" : lookupTablePath({ "standard" : "ISO", "engagement" : "75%", "pitch" : "0.75 mm", "size" : "M4", "type" : "Tapped" }), "holeDiameter" : 3.2 * mm, "holeDepth" : 20 * mm, "startFromSketch" : true, "locations" : qUnion([Q0]), "scope" : qUnion([Q1])});
        }
        {
            var Q0;
            Q0=makeQuery(id+"F3.boolean.opBoolean","COPY",FACE,{"derivedFrom":makeQuery(id+"F3.opExtrude","SWEPT_FACE",FACE,{"disambiguationData":[OSD([sQuery(id+"F2.wireOp",EDGE,"E42")])]})});
            var sketch = newSketch(context, id + "F35", { "sketchPlane" : qUnion([Q0])});
            skCircle(sketch, "E67", {"center": v(12.5, 0) * mm, "radius": 1.75 * mm});
            skPoint(sketch, "E67.centerSnap0", {"position": v(12.5, -10.1) * mm});
            skSolve(sketch);
        }
        {
            var Q0;
            Q0=sQuery(id+"F35.wireOp",VERTEX,"E67.center");
            var Q1;
            Q1=makeQuery(id+"F1.opExtrude","SWEPT_BODY",BODY,{"disambiguationData":[OSD([sQuery(id+"F0.wireOp",EDGE,"E0"),sQuery(id+"F0.wireOp",EDGE,"E1")])]});
            hole(context, id + "F36", {"style" : HoleStyle.SIMPLE, "endStyle" : HoleEndStyle.BLIND, "standardTappedOrClearance" : lookupTablePath({ "standard" : "ISO", "engagement" : "75%", "pitch" : "0.75 mm", "size" : "M4", "type" : "Tapped" }), "standardBlindInLast" : lookupTablePath({ "standard" : "ISO", "engagement" : "75%", "pitch" : "0.75 mm", "size" : "M4", "type" : "Tapped" }), "holeDiameter" : 3.2 * mm, "holeDepth" : 20 * mm, "startFromSketch" : true, "locations" : qUnion([Q0]), "scope" : qUnion([Q1])});
        }
        {
            var Q0;
            Q0=makeQuery(id+"F3.boolean.opBoolean","COPY",FACE,{"derivedFrom":makeQuery(id+"F3.opExtrude","SWEPT_FACE",FACE,{"disambiguationData":[OSD([sQuery(id+"F2.wireOp",EDGE,"E44")])]})});
            var sketch = newSketch(context, id + "F37", { "sketchPlane" : qUnion([Q0])});
            skCircle(sketch, "E68", {"center": v(12.5, 0) * mm, "radius": 1.75 * mm});
            skPoint(sketch, "E68.centerSnap0", {"position": v(12.5, -10.1) * mm});
            skSolve(sketch);
        }
        {
            var Q0;
            Q0=sQuery(id+"F37.wireOp",VERTEX,"E68.center");
            var Q1;
            Q1=makeQuery(id+"F1.opExtrude","SWEPT_BODY",BODY,{"disambiguationData":[OSD([sQuery(id+"F0.wireOp",EDGE,"E0"),sQuery(id+"F0.wireOp",EDGE,"E1")])]});
            hole(context, id + "F38", {"style" : HoleStyle.SIMPLE, "endStyle" : HoleEndStyle.BLIND, "standardTappedOrClearance" : lookupTablePath({ "standard" : "ISO", "engagement" : "75%", "pitch" : "0.75 mm", "size" : "M4", "type" : "Tapped" }), "standardBlindInLast" : lookupTablePath({ "standard" : "ISO", "engagement" : "75%", "pitch" : "0.75 mm", "size" : "M4", "type" : "Tapped" }), "holeDiameter" : 3.2 * mm, "holeDepth" : 20 * mm, "startFromSketch" : true, "locations" : qUnion([Q0]), "scope" : qUnion([Q1])});
        }
        {
            var Q0;
            Q0=makeQuery(id+"F3.boolean.opBoolean","COPY",FACE,{"derivedFrom":makeQuery(id+"F3.opExtrude","SWEPT_FACE",FACE,{"disambiguationData":[OSD([sQuery(id+"F2.wireOp",EDGE,"E46")])]})});
            var sketch = newSketch(context, id + "F39", { "sketchPlane" : qUnion([Q0])});
            skCircle(sketch, "E69", {"center": v(0, -12.5) * mm, "radius": 1.75 * mm});
            skPoint(sketch, "E69.centerSnap0", {"position": v(-10.1, -12.5) * mm});
            skPoint(sketch, "E69.centerSnap1", {"position": v(0, 0) * mm});
            skSolve(sketch);
        }
        {
            var Q0;
            Q0=sQuery(id+"F39.wireOp",VERTEX,"E69.center");
            var Q1;
            Q1=makeQuery(id+"F1.opExtrude","SWEPT_BODY",BODY,{"disambiguationData":[OSD([sQuery(id+"F0.wireOp",EDGE,"E0"),sQuery(id+"F0.wireOp",EDGE,"E1")])]});
            hole(context, id + "F40", {"style" : HoleStyle.SIMPLE, "endStyle" : HoleEndStyle.BLIND, "standardTappedOrClearance" : lookupTablePath({ "standard" : "ISO", "engagement" : "75%", "pitch" : "0.75 mm", "size" : "M4", "type" : "Tapped" }), "standardBlindInLast" : lookupTablePath({ "standard" : "ISO", "engagement" : "75%", "pitch" : "0.75 mm", "size" : "M4", "type" : "Tapped" }), "holeDiameter" : 3.2 * mm, "holeDepth" : 20 * mm, "startFromSketch" : true, "locations" : qUnion([Q0]), "scope" : qUnion([Q1])});
        }
        {
            var Q0;
            Q0=makeQuery(id+"F3.boolean.opBoolean","COPY",FACE,{"derivedFrom":makeQuery(id+"F3.opExtrude","SWEPT_FACE",FACE,{"disambiguationData":[OSD([sQuery(id+"F2.wireOp",EDGE,"E48")])]})});
            var sketch = newSketch(context, id + "F41", { "sketchPlane" : qUnion([Q0])});
            skCircle(sketch, "E70", {"center": v(0, -12.5) * mm, "radius": 1.75 * mm});
            skPoint(sketch, "E70.centerSnap0", {"position": v(-10.1, -12.5) * mm});
            skPoint(sketch, "E70.centerSnap1", {"position": v(0, 0) * mm});
            skSolve(sketch);
        }
        {
            var Q0;
            Q0=sQuery(id+"F41.wireOp",VERTEX,"E70.center");
            var Q1;
            Q1=makeQuery(id+"F1.opExtrude","SWEPT_BODY",BODY,{"disambiguationData":[OSD([sQuery(id+"F0.wireOp",EDGE,"E0"),sQuery(id+"F0.wireOp",EDGE,"E1")])]});
            hole(context, id + "F42", {"style" : HoleStyle.SIMPLE, "endStyle" : HoleEndStyle.BLIND, "standardTappedOrClearance" : lookupTablePath({ "standard" : "ISO", "engagement" : "75%", "pitch" : "0.75 mm", "size" : "M4", "type" : "Tapped" }), "standardBlindInLast" : lookupTablePath({ "standard" : "ISO", "engagement" : "75%", "pitch" : "0.75 mm", "size" : "M4", "type" : "Tapped" }), "holeDiameter" : 3.2 * mm, "holeDepth" : 20 * mm, "startFromSketch" : true, "locations" : qUnion([Q0]), "scope" : qUnion([Q1])});
        }
        {
            var Q0;
            Q0=makeQuery(id+"F3.boolean.opBoolean","COPY",FACE,{"derivedFrom":makeQuery(id+"F3.opExtrude","SWEPT_FACE",FACE,{"disambiguationData":[OSD([sQuery(id+"F2.wireOp",EDGE,"E49")])]})});
            var sketch = newSketch(context, id + "F43", { "sketchPlane" : qUnion([Q0])});
            skCircle(sketch, "E71", {"center": v(0, -12.5) * mm, "radius": 1.75 * mm});
            skPoint(sketch, "E71.centerSnap0", {"position": v(-9.38, -12.5) * mm});
            skSolve(sketch);
        }
        {
            var Q0;
            Q0=sQuery(id+"F43.wireOp",VERTEX,"E71.center");
            var Q1;
            Q1=makeQuery(id+"F1.opExtrude","SWEPT_BODY",BODY,{"disambiguationData":[OSD([sQuery(id+"F0.wireOp",EDGE,"E0"),sQuery(id+"F0.wireOp",EDGE,"E1")])]});
            hole(context, id + "F44", {"style" : HoleStyle.SIMPLE, "endStyle" : HoleEndStyle.BLIND, "standardTappedOrClearance" : lookupTablePath({ "standard" : "ISO", "engagement" : "75%", "pitch" : "0.75 mm", "size" : "M4", "type" : "Tapped" }), "standardBlindInLast" : lookupTablePath({ "standard" : "ISO", "engagement" : "75%", "pitch" : "0.75 mm", "size" : "M4", "type" : "Tapped" }), "holeDiameter" : 3.2 * mm, "holeDepth" : 20 * mm, "startFromSketch" : true, "locations" : qUnion([Q0]), "scope" : qUnion([Q1])});
        }
        {
            var Q0;
            Q0=makeQuery(id+"F3.boolean.opBoolean","COPY",FACE,{"derivedFrom":makeQuery(id+"F3.opExtrude","SWEPT_FACE",FACE,{"disambiguationData":[OSD([sQuery(id+"F2.wireOp",EDGE,"E4")])]})});
            var sketch = newSketch(context, id + "F45", { "sketchPlane" : qUnion([Q0])});
            skCircle(sketch, "E72", {"center": v(0, -12.5) * mm, "radius": 1.75 * mm});
            skPoint(sketch, "E72.centerSnap0", {"position": v(-10.1, -12.5) * mm});
            skSolve(sketch);
        }
        {
            var Q0;
            Q0=sQuery(id+"F45.wireOp",VERTEX,"E72.center");
            var Q1;
            Q1=makeQuery(id+"F1.opExtrude","SWEPT_BODY",BODY,{"disambiguationData":[OSD([sQuery(id+"F0.wireOp",EDGE,"E0"),sQuery(id+"F0.wireOp",EDGE,"E1")])]});
            hole(context, id + "F46", {"style" : HoleStyle.SIMPLE, "endStyle" : HoleEndStyle.BLIND, "standardTappedOrClearance" : lookupTablePath({ "standard" : "ISO", "engagement" : "75%", "pitch" : "0.75 mm", "size" : "M4", "type" : "Tapped" }), "standardBlindInLast" : lookupTablePath({ "standard" : "ISO", "engagement" : "75%", "pitch" : "0.75 mm", "size" : "M4", "type" : "Tapped" }), "holeDiameter" : 3.2 * mm, "holeDepth" : 20 * mm, "startFromSketch" : true, "locations" : qUnion([Q0]), "scope" : qUnion([Q1])});
        }
        {
            var Q0;
            Q0=makeQuery(id+"F3.boolean.opBoolean","COPY",FACE,{"derivedFrom":makeQuery(id+"F3.opExtrude","SWEPT_FACE",FACE,{"disambiguationData":[OSD([sQuery(id+"F2.wireOp",EDGE,"E6")])]})});
            var sketch = newSketch(context, id + "F47", { "sketchPlane" : qUnion([Q0])});
            skCircle(sketch, "E73", {"center": v(0, -12.5) * mm, "radius": 1.75 * mm});
            skPoint(sketch, "E73.centerSnap0", {"position": v(-10.1, -12.5) * mm});
            skSolve(sketch);
        }
        {
            var Q0;
            Q0=sQuery(id+"F47.wireOp",VERTEX,"E73.center");
            var Q1;
            Q1=makeQuery(id+"F1.opExtrude","SWEPT_BODY",BODY,{"disambiguationData":[OSD([sQuery(id+"F0.wireOp",EDGE,"E0"),sQuery(id+"F0.wireOp",EDGE,"E1")])]});
            hole(context, id + "F48", {"style" : HoleStyle.SIMPLE, "endStyle" : HoleEndStyle.BLIND, "standardTappedOrClearance" : lookupTablePath({ "standard" : "ISO", "engagement" : "75%", "pitch" : "0.75 mm", "size" : "M4", "type" : "Tapped" }), "standardBlindInLast" : lookupTablePath({ "standard" : "ISO", "engagement" : "75%", "pitch" : "0.75 mm", "size" : "M4", "type" : "Tapped" }), "holeDiameter" : 3.2 * mm, "holeDepth" : 20 * mm, "startFromSketch" : true, "locations" : qUnion([Q0]), "scope" : qUnion([Q1])});
        }
        {
            var Q0;
            Q0=makeQuery(id+"F3.boolean.opBoolean","COPY",FACE,{"derivedFrom":makeQuery(id+"F3.opExtrude","SWEPT_FACE",FACE,{"disambiguationData":[OSD([sQuery(id+"F2.wireOp",EDGE,"E8")])]})});
            var sketch = newSketch(context, id + "F49", { "sketchPlane" : qUnion([Q0])});
            skCircle(sketch, "E74", {"center": v(0, -12.5) * mm, "radius": 1.75 * mm});
            skPoint(sketch, "E74.centerSnap0", {"position": v(-10.1, -12.5) * mm});
            skPoint(sketch, "E74.centerSnap1", {"position": v(0, 0) * mm});
            skSolve(sketch);
        }
        {
            var Q0;
            Q0=sQuery(id+"F49.wireOp",VERTEX,"E74.center");
            var Q1;
            Q1=makeQuery(id+"F1.opExtrude","SWEPT_BODY",BODY,{"disambiguationData":[OSD([sQuery(id+"F0.wireOp",EDGE,"E0"),sQuery(id+"F0.wireOp",EDGE,"E1")])]});
            hole(context, id + "F50", {"style" : HoleStyle.SIMPLE, "endStyle" : HoleEndStyle.BLIND, "standardTappedOrClearance" : lookupTablePath({ "standard" : "ISO", "engagement" : "75%", "pitch" : "0.75 mm", "size" : "M4", "type" : "Tapped" }), "standardBlindInLast" : lookupTablePath({ "standard" : "ISO", "engagement" : "75%", "pitch" : "0.75 mm", "size" : "M4", "type" : "Tapped" }), "holeDiameter" : 3.2 * mm, "holeDepth" : 20 * mm, "startFromSketch" : true, "locations" : qUnion([Q0]), "scope" : qUnion([Q1])});
        }
        {
            var Q0;
            Q0=makeQuery(id+"F3.boolean.opBoolean","COPY",FACE,{"derivedFrom":makeQuery(id+"F3.opExtrude","SWEPT_FACE",FACE,{"disambiguationData":[OSD([sQuery(id+"F2.wireOp",EDGE,"E10")])]})});
            var sketch = newSketch(context, id + "F51", { "sketchPlane" : qUnion([Q0])});
            skCircle(sketch, "E75", {"center": v(-12.5, 0) * mm, "radius": 1.75 * mm});
            skPoint(sketch, "E75.centerSnap0", {"position": v(-12.5, 10.1) * mm});
            skPoint(sketch, "E75.centerSnap1", {"position": v(0, 0) * mm});
            skSolve(sketch);
        }
        {
            var Q0;
            Q0=sQuery(id+"F51.wireOp",VERTEX,"E75.center");
            var Q1;
            Q1=makeQuery(id+"F1.opExtrude","SWEPT_BODY",BODY,{"disambiguationData":[OSD([sQuery(id+"F0.wireOp",EDGE,"E0"),sQuery(id+"F0.wireOp",EDGE,"E1")])]});
            hole(context, id + "F52", {"style" : HoleStyle.SIMPLE, "endStyle" : HoleEndStyle.BLIND, "standardTappedOrClearance" : lookupTablePath({ "standard" : "ISO", "engagement" : "75%", "pitch" : "0.75 mm", "size" : "M4", "type" : "Tapped" }), "standardBlindInLast" : lookupTablePath({ "standard" : "ISO", "engagement" : "75%", "pitch" : "0.75 mm", "size" : "M4", "type" : "Tapped" }), "holeDiameter" : 3.2 * mm, "holeDepth" : 20 * mm, "startFromSketch" : true, "locations" : qUnion([Q0]), "scope" : qUnion([Q1])});
        }
        {
            var Q0;
            Q0=makeQuery(id+"F3.boolean.opBoolean","COPY",FACE,{"derivedFrom":makeQuery(id+"F3.opExtrude","SWEPT_FACE",FACE,{"disambiguationData":[OSD([sQuery(id+"F2.wireOp",EDGE,"E12")])]})});
            var sketch = newSketch(context, id + "F53", { "sketchPlane" : qUnion([Q0])});
            skCircle(sketch, "E76", {"center": v(-12.5, 0) * mm, "radius": 1.75 * mm});
            skPoint(sketch, "E76.centerSnap0", {"position": v(-12.5, 10.1) * mm});
            skSolve(sketch);
        }
        {
            var Q0;
            Q0=sQuery(id+"F53.wireOp",VERTEX,"E76.center");
            var Q1;
            Q1=makeQuery(id+"F1.opExtrude","SWEPT_BODY",BODY,{"disambiguationData":[OSD([sQuery(id+"F0.wireOp",EDGE,"E0"),sQuery(id+"F0.wireOp",EDGE,"E1")])]});
            hole(context, id + "F54", {"style" : HoleStyle.SIMPLE, "endStyle" : HoleEndStyle.BLIND, "standardTappedOrClearance" : lookupTablePath({ "standard" : "ISO", "engagement" : "75%", "pitch" : "0.75 mm", "size" : "M4", "type" : "Tapped" }), "standardBlindInLast" : lookupTablePath({ "standard" : "ISO", "engagement" : "75%", "pitch" : "0.75 mm", "size" : "M4", "type" : "Tapped" }), "holeDiameter" : 3.2 * mm, "holeDepth" : 20 * mm, "startFromSketch" : true, "locations" : qUnion([Q0]), "scope" : qUnion([Q1])});
        }
        {
            var Q0;
            Q0=qCreatedBy(makeId("Right.planeOp"),FACE);
            var sketch = newSketch(context, id + "F55", { "sketchPlane" : qUnion([Q0])});
            skCircle(sketch, "E77", {"center": v(-12.5, -0.36) * mm, "radius": 2.5 * mm});
            skSolve(sketch);
        }
        {
            var Q0;
            Q0=sQuery(id+"F55.wireOp",VERTEX,"E77.center");
            var Q1;
            Q1=makeQuery(id+"F1.opExtrude","SWEPT_BODY",BODY,{"disambiguationData":[OSD([sQuery(id+"F0.wireOp",EDGE,"E0"),sQuery(id+"F0.wireOp",EDGE,"E1")])]});
            hole(context, id + "F56", {"style" : HoleStyle.SIMPLE, "endStyle" : HoleEndStyle.BLIND, "standardTappedOrClearance" : lookupTablePath({ "standard" : "ISO", "engagement" : "75%", "pitch" : "1 mm", "size" : "M6", "type" : "Tapped" }), "standardBlindInLast" : lookupTablePath({ "standard" : "ISO", "engagement" : "75%", "pitch" : "1 mm", "size" : "M6", "type" : "Tapped" }), "holeDiameter" : 5 * mm, "holeDepth" : 100 * mm, "startFromSketch" : true, "locations" : qUnion([Q0]), "scope" : qUnion([Q1]), "majorDiameter" : 6 * mm});
        }
        {
            var Q0;
            Q0=qCreatedBy(makeId("Right.planeOp"),FACE);
            var sketch = newSketch(context, id + "F57", { "sketchPlane" : qUnion([Q0])});
            skCircle(sketch, "E78", {"center": v(-12.55, 0) * mm, "radius": 2.5 * mm});
            skSolve(sketch);
        }
        {
            var Q0;
            Q0=sQuery(id+"F57.wireOp",VERTEX,"E78.center");
            var Q1;
            Q1=makeQuery(id+"F1.opExtrude","SWEPT_BODY",BODY,{"disambiguationData":[OSD([sQuery(id+"F0.wireOp",EDGE,"E0"),sQuery(id+"F0.wireOp",EDGE,"E1")])]});
            hole(context, id + "F58", {"style" : HoleStyle.SIMPLE, "endStyle" : HoleEndStyle.BLIND, "oppositeDirection" : true, "standardTappedOrClearance" : lookupTablePath({ "standard" : "ISO", "engagement" : "75%", "pitch" : "1 mm", "size" : "M6", "type" : "Tapped" }), "standardBlindInLast" : lookupTablePath({ "standard" : "ISO", "engagement" : "75%", "pitch" : "1 mm", "size" : "M6", "type" : "Tapped" }), "holeDiameter" : 5 * mm, "holeDepth" : 100 * mm, "startFromSketch" : true, "locations" : qUnion([Q0]), "scope" : qUnion([Q1]), "majorDiameter" : 6 * mm});
        }
    });
